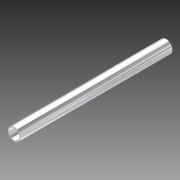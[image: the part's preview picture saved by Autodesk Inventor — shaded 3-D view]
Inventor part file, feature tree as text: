
AUTODESK INVENTOR PART (.ipt)
format: ipt  version: 2011 (Build 150239000, 239)  size: 71,680 bytes
history: native  units: in
note: dims shown in document units (in); Inventor stores cm internally (conversion verified against a paired STEP export)
features: extrude x1, sketch x1
ambient origin geometry x8: Origin, YZ Plane, XZ Plane, XY Plane, X Axis, Y Axis, Z Axis, Center Point
bodies: Solid1 (feature_tree)
feature tree (2):
  extrude  "Extrusion1"  Depth=0.95in
  sketch  "Sketch1"  dims[d0=1.125in d1=0.95in d2=13.5in d3=0.0in]
